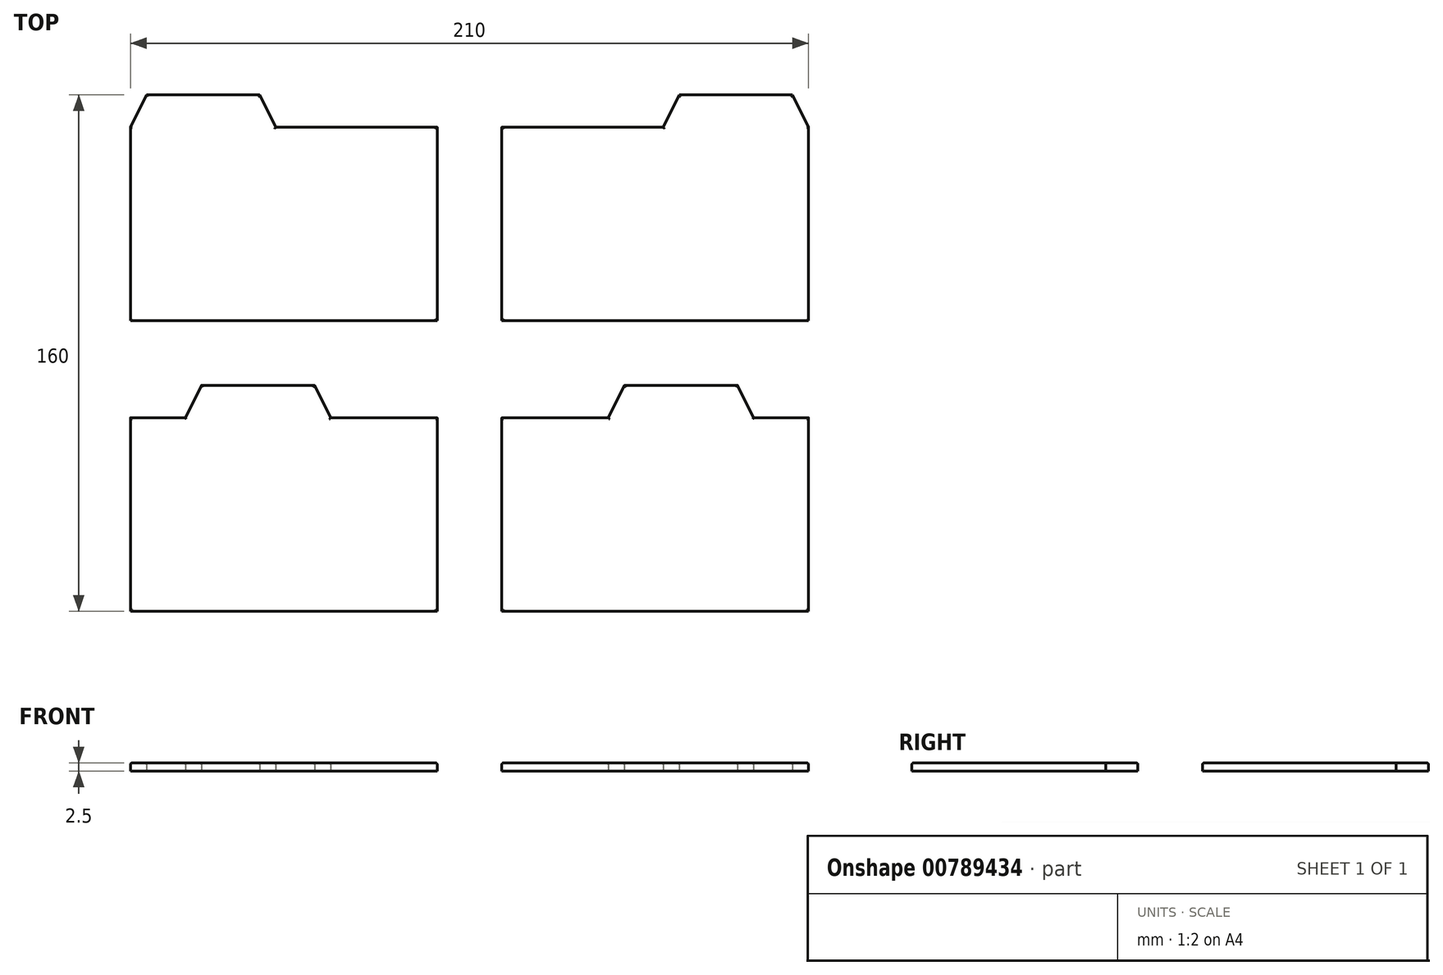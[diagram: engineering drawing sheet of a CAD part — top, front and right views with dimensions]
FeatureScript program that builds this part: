
annotation { "Feature Type Name" : "Feature", "Feature Type Description" : "" }
export const myFeature = defineFeature(function(context is Context, id is Id, definition is map)
    precondition{}
    {
        {
            var Q0;
            Q0=qCreatedBy(makeId("Top.planeOp"),FACE);
            var sketch = newSketch(context, id + "F0", { "sketchPlane" : qUnion([Q0])});
            skLineSegment(sketch, "E0.bottom", {"start": v(47.5, 30) * mm, "end": v(-47.5, 30) * mm});
            skLineSegment(sketch, "E0.top", {"start": v(47.5, -30) * mm, "end": v(-47.5, -30) * mm});
            skLineSegment(sketch, "E0.left", {"start": v(47.5, 30) * mm, "end": v(47.5, -30) * mm});
            skLineSegment(sketch, "E0.right", {"start": v(-47.5, 30) * mm, "end": v(-47.5, -30) * mm});
            skPoint(sketch, "E0.middle", {"position": v(0, 0) * mm});
            skLineSegment(sketch, "E1", {"start": v(-47.5, 30) * mm, "end": v(-42.5, 40) * mm});
            skLineSegment(sketch, "E2", {"start": v(-42.5, 40) * mm, "end": v(-7.5, 40) * mm});
            skLineSegment(sketch, "E3", {"start": v(-7.5, 40) * mm, "end": v(-2.5, 30) * mm});
            skLineSegment(sketch, "E4", {"start": v(57.5, 39.25) * mm, "end": v(57.5, -116.59) * mm, "construction": true});
            skLineSegment(sketch, "E5.MirrorCS", {"start": v(122.5, 40) * mm, "end": v(117.5, 30) * mm});
            skPoint(sketch, "E6.MirrorP", {"position": v(115, 0) * mm});
            skLineSegment(sketch, "E7.MirrorCS", {"start": v(162.5, 30) * mm, "end": v(162.5, -30) * mm});
            skLineSegment(sketch, "E8.MirrorCS", {"start": v(67.5, 30) * mm, "end": v(67.5, -30) * mm});
            skLineSegment(sketch, "E9.MirrorCS", {"start": v(67.5, -30) * mm, "end": v(162.5, -30) * mm});
            skLineSegment(sketch, "E10.MirrorCS", {"start": v(162.5, 30) * mm, "end": v(157.5, 40) * mm});
            skLineSegment(sketch, "E11.MirrorCS", {"start": v(67.5, 30) * mm, "end": v(162.5, 30) * mm});
            skLineSegment(sketch, "E12.MirrorCS", {"start": v(157.5, 40) * mm, "end": v(122.5, 40) * mm});
            skLineSegment(sketch, "E13", {"start": v(-108.62, -45) * mm, "end": v(207.78, -45) * mm, "construction": true});
            skLineSegment(sketch, "E14.MirrorCS", {"start": v(-47.5, -120) * mm, "end": v(-47.5, -60) * mm});
            skLineSegment(sketch, "E15.MirrorCS", {"start": v(47.5, -60) * mm, "end": v(-47.5, -60) * mm});
            skLineSegment(sketch, "E16.MirrorCS", {"start": v(47.5, -120) * mm, "end": v(47.5, -60) * mm});
            skLineSegment(sketch, "E17.MirrorCS", {"start": v(47.5, -120) * mm, "end": v(-47.5, -120) * mm});
            skPoint(sketch, "E18.MirrorP", {"position": v(0, -90) * mm});
            skLineSegment(sketch, "E19", {"start": v(-30.5, -60) * mm, "end": v(-25.5, -50) * mm});
            skLineSegment(sketch, "E20", {"start": v(-25.5, -50) * mm, "end": v(9.5, -50) * mm});
            skLineSegment(sketch, "E21", {"start": v(9.5, -50) * mm, "end": v(14.5, -60) * mm});
            skLineSegment(sketch, "E22.MirrorCS", {"start": v(162.5, -120) * mm, "end": v(162.5, -60) * mm});
            skLineSegment(sketch, "E23.MirrorCS", {"start": v(105.5, -50) * mm, "end": v(100.5, -60) * mm});
            skLineSegment(sketch, "E24.MirrorCS", {"start": v(140.5, -50) * mm, "end": v(105.5, -50) * mm});
            skLineSegment(sketch, "E25.MirrorCS", {"start": v(67.5, -120) * mm, "end": v(162.5, -120) * mm});
            skLineSegment(sketch, "E26.MirrorCS", {"start": v(67.5, -60) * mm, "end": v(162.5, -60) * mm});
            skLineSegment(sketch, "E27.MirrorCS", {"start": v(67.5, -120) * mm, "end": v(67.5, -60) * mm});
            skLineSegment(sketch, "E28.MirrorCS", {"start": v(145.5, -60) * mm, "end": v(140.5, -50) * mm});
            skPoint(sketch, "E29.MirrorP", {"position": v(115, -90) * mm});
            skSolve(sketch);
        }
        {
            var Q0;
            Q0 = qSketchRegion(id + "F0", true);
            extrude(context, id + "F1", {"entities" : qUnion([Q0]), "depth" : 2.5 * mm, "offsetDistance" : 25 * mm});
        }
        {
            var Q0;
            Q0=makeQuery(id+"F1.opExtrude","CAP_EDGE",EDGE,{"disambiguationData":[OSD([sQuery(id+"F0.wireOp",EDGE,"E1")])],"isStart":false});
            var Q1;
            Q1=makeQuery(id+"F1.opExtrude","CAP_EDGE",EDGE,{"disambiguationData":[OSD([sQuery(id+"F0.wireOp",EDGE,"E2")])],"isStart":false});
            var Q2;
            Q2=makeQuery(id+"F1.opExtrude","CAP_EDGE",EDGE,{"disambiguationData":[OSD([sQuery(id+"F0.wireOp",EDGE,"E3")])],"isStart":false});
            var Q3;
            Q3=makeQuery(id+"F1.opExtrude","CAP_EDGE",EDGE,{"disambiguationData":[OSD([sQuery(id+"F0.wireOp",EDGE,"E0.bottom")])],"isStart":false});
            var Q4;
            Q4=makeQuery(id+"F1.opExtrude","CAP_EDGE",EDGE,{"disambiguationData":[OSD([sQuery(id+"F0.wireOp",EDGE,"E0.left")])],"isStart":false});
            var Q5;
            Q5=makeQuery(id+"F1.opExtrude","CAP_EDGE",EDGE,{"disambiguationData":[OSD([sQuery(id+"F0.wireOp",EDGE,"E0.top")])],"isStart":false});
            var Q6;
            Q6=makeQuery(id+"F1.opExtrude","CAP_EDGE",EDGE,{"disambiguationData":[OSD([sQuery(id+"F0.wireOp",EDGE,"E0.right")])],"isStart":false});
            var Q7;
            Q7=makeQuery(id+"F1.opExtrude","CAP_EDGE",EDGE,{"disambiguationData":[OSD([sQuery(id+"F0.wireOp",EDGE,"E8.MirrorCS")])],"isStart":false});
            var Q8;
            Q8=makeQuery(id+"F1.opExtrude","CAP_EDGE",EDGE,{"disambiguationData":[OSD([sQuery(id+"F0.wireOp",EDGE,"E11.MirrorCS")])],"isStart":false});
            var Q9;
            Q9=makeQuery(id+"F1.opExtrude","CAP_EDGE",EDGE,{"disambiguationData":[OSD([sQuery(id+"F0.wireOp",EDGE,"E5.MirrorCS")])],"isStart":false});
            var Q10;
            Q10=makeQuery(id+"F1.opExtrude","CAP_EDGE",EDGE,{"disambiguationData":[OSD([sQuery(id+"F0.wireOp",EDGE,"E12.MirrorCS")])],"isStart":false});
            var Q11;
            Q11=makeQuery(id+"F1.opExtrude","CAP_EDGE",EDGE,{"disambiguationData":[OSD([sQuery(id+"F0.wireOp",EDGE,"E10.MirrorCS")])],"isStart":false});
            var Q12;
            Q12=makeQuery(id+"F1.opExtrude","CAP_EDGE",EDGE,{"disambiguationData":[OSD([sQuery(id+"F0.wireOp",EDGE,"E7.MirrorCS")])],"isStart":false});
            var Q13;
            Q13=makeQuery(id+"F1.opExtrude","CAP_EDGE",EDGE,{"disambiguationData":[OSD([sQuery(id+"F0.wireOp",EDGE,"E9.MirrorCS")])],"isStart":false});
            var Q14;
            Q14=makeQuery(id+"F1.opExtrude","CAP_EDGE",EDGE,{"disambiguationData":[OSD([sQuery(id+"F0.wireOp",EDGE,"E14.MirrorCS")])],"isStart":false});
            var Q15;
            {var subQ0=sQuery(id+"F0.wireOp",EDGE,"E15.MirrorCS");Q15=makeQuery(id+"F1.opExtrude","CAP_EDGE",EDGE,{"disambiguationData":[OSD([subQ0]),TDD([makeQuery(id+"F0.imprint","IMPRINT",EDGE,{"disambiguationData":[TD([[makeQuery(id+"F0.imprint","INTERSECT",VERTEX,{"derivedFrom":[sQuery(id+"F0.wireOp",EDGE,"E14.MirrorCS"),subQ0]}),1.0]])],"derivedFrom":subQ0})])],"isStart":false});}
            var Q16;
            Q16=makeQuery(id+"F1.opExtrude","CAP_EDGE",EDGE,{"disambiguationData":[OSD([sQuery(id+"F0.wireOp",EDGE,"E19")])],"isStart":false});
            var Q17;
            Q17=makeQuery(id+"F1.opExtrude","CAP_EDGE",EDGE,{"disambiguationData":[OSD([sQuery(id+"F0.wireOp",EDGE,"E20")])],"isStart":false});
            var Q18;
            Q18=makeQuery(id+"F1.opExtrude","CAP_EDGE",EDGE,{"disambiguationData":[OSD([sQuery(id+"F0.wireOp",EDGE,"E21")])],"isStart":false});
            var Q19;
            {var subQ0=sQuery(id+"F0.wireOp",EDGE,"E15.MirrorCS");Q19=makeQuery(id+"F1.opExtrude","CAP_EDGE",EDGE,{"disambiguationData":[OSD([subQ0]),TDD([makeQuery(id+"F0.imprint","IMPRINT",EDGE,{"disambiguationData":[TD([[makeQuery(id+"F0.imprint","INTERSECT",VERTEX,{"derivedFrom":[subQ0,sQuery(id+"F0.wireOp",EDGE,"E16.MirrorCS")]}),-1.0]])],"derivedFrom":subQ0})])],"isStart":false});}
            var Q20;
            Q20=makeQuery(id+"F1.opExtrude","CAP_EDGE",EDGE,{"disambiguationData":[OSD([sQuery(id+"F0.wireOp",EDGE,"E16.MirrorCS")])],"isStart":false});
            var Q21;
            Q21=makeQuery(id+"F1.opExtrude","CAP_EDGE",EDGE,{"disambiguationData":[OSD([sQuery(id+"F0.wireOp",EDGE,"E17.MirrorCS")])],"isStart":false});
            var Q22;
            Q22=makeQuery(id+"F1.opExtrude","CAP_EDGE",EDGE,{"disambiguationData":[OSD([sQuery(id+"F0.wireOp",EDGE,"E27.MirrorCS")])],"isStart":false});
            var Q23;
            {var subQ0=sQuery(id+"F0.wireOp",EDGE,"E26.MirrorCS");Q23=makeQuery(id+"F1.opExtrude","CAP_EDGE",EDGE,{"disambiguationData":[OSD([subQ0]),TDD([makeQuery(id+"F0.imprint","IMPRINT",EDGE,{"disambiguationData":[TD([[makeQuery(id+"F0.imprint","INTERSECT",VERTEX,{"derivedFrom":[sQuery(id+"F0.wireOp",EDGE,"E23.MirrorCS"),subQ0]}),1.0]])],"derivedFrom":subQ0})])],"isStart":false});}
            var Q24;
            Q24=makeQuery(id+"F1.opExtrude","CAP_EDGE",EDGE,{"disambiguationData":[OSD([sQuery(id+"F0.wireOp",EDGE,"E23.MirrorCS")])],"isStart":false});
            var Q25;
            Q25=makeQuery(id+"F1.opExtrude","CAP_EDGE",EDGE,{"disambiguationData":[OSD([sQuery(id+"F0.wireOp",EDGE,"E24.MirrorCS")])],"isStart":false});
            var Q26;
            Q26=makeQuery(id+"F1.opExtrude","CAP_EDGE",EDGE,{"disambiguationData":[OSD([sQuery(id+"F0.wireOp",EDGE,"E28.MirrorCS")])],"isStart":false});
            var Q27;
            {var subQ0=sQuery(id+"F0.wireOp",EDGE,"E26.MirrorCS");Q27=makeQuery(id+"F1.opExtrude","CAP_EDGE",EDGE,{"disambiguationData":[OSD([subQ0]),TDD([makeQuery(id+"F0.imprint","IMPRINT",EDGE,{"disambiguationData":[TD([[makeQuery(id+"F0.imprint","INTERSECT",VERTEX,{"derivedFrom":[sQuery(id+"F0.wireOp",EDGE,"E22.MirrorCS"),subQ0]}),1.0]])],"derivedFrom":subQ0})])],"isStart":false});}
            var Q28;
            Q28=makeQuery(id+"F1.opExtrude","CAP_EDGE",EDGE,{"disambiguationData":[OSD([sQuery(id+"F0.wireOp",EDGE,"E22.MirrorCS")])],"isStart":false});
            var Q29;
            Q29=makeQuery(id+"F1.opExtrude","CAP_EDGE",EDGE,{"disambiguationData":[OSD([sQuery(id+"F0.wireOp",EDGE,"E25.MirrorCS")])],"isStart":false});
            fillet(context, id + "F2", {"entities" : qUnion([Q0, Q1, Q2, Q3, Q4, Q5, Q6, Q7, Q8, Q9, Q10, Q11, Q12, Q13, Q14, Q15, Q16, Q17, Q18, Q19, Q20, Q21, Q22, Q23, Q24, Q25, Q26, Q27, Q28, Q29]), "radius" : 0.5 * mm, "tangentPropagation" : true, "allowEdgeOverflow" : false});
        }
    });
